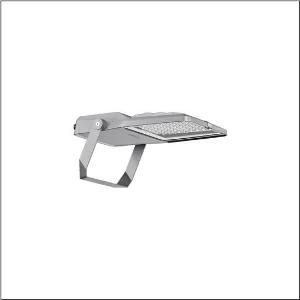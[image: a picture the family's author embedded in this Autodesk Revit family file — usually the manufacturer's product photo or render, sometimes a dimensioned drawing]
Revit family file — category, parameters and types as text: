
# Revit family: floodlight_fl_21_iq_mini___pl33t_5xa7771d4f1a_3e9c
name_source: partatom
category: Lighting Fixtures
units: mm (PartAtom-declared; Revit-internal decimal feet)

## family parameters
Cut with Voids When Loaded = No
Host = Face
Light Source = No
Part Type = Normal
Room Calculation Point = No
Round Connector Dimension = Use Diameter
Shared = No

## types (1)
- --- (1 x LED, 18390 lm, 143 W, 4000K)
    Apparent Load = 143 VA
    CIE Flux Codes = 26 75 99 100 100
    Color Rendering = 70
    Color Temperature = 4000K
    Default Elevation = 1800 mm
    Description = Floodlight FL 21 iQ mini, floodlight, primary light control with lens, of PMMA, primary optical cover: protective disc, of toughened safety glass, transparent, light distribution: PL33T, light emission: direct distribution, installation type: surface-mounted, LED, High Power LED, rated luminous flux: 18.390lm, luminous efficacy: 129lm/W, light colour: 740, colour temperature: 4000K, control: Auto-Match, Temp-Guard, Lumen-Switch, Night-Set, Smart-Wire, Light-Fading, Desk-Remote (wireless, voltage-free reading and setting of iQ features in the workshop via application-optimized NFC function/RFID function), optimised constant luminous flux control (CLO 2.0), with terminal, 6-pole, mains connection: 220..240V, AC, 50/60Hz, start of lifetime: 143W, end of service life: 152W, reduction: 61W, luminaire housing, of diecast aluminium, powder-coated, Siteco® metallic grey (DB 702S), corrosivity category C5 mid according to DIN EN ISO 12944, sealing non-destructively replaceable, mounting bracket, of steel, galvanised, powder-coated, Siteco® metallic grey (DB 702S), protection rating (complete): IP66, insulation class (complete): insulation class II (safety insulation), certification: CE, ENEC, VDE, protection symbol: D, impact resistance: IK08, permissible operating ambient temperature: -40..+40°C, permissible operating ambient temperature for outdoor applications: -40..+50°C, standard: DIN EN 12944, LABS conformity tested according to VDMA 24364:2018-05, packaging unit: 1 piece

Light Distribution: PL33T
    Height = 70 mm
    Lamp = 1 x LED
    Lamp Light Flux = 18390 lm
    Lamp Power = 143 W
    Lamp count = 1
    Length = 485 mm
    Luminous efficacy = 129 lm/W
    Manufacturer = Siteco
    ModVariant = No
    Model = 5XA7771D4F1A
    Number of Poles = 1
    OnlyDefault = Yes
    Power Factor = 1
    Product Name = Floodlight FL 21 iQ mini | PL33T
    Product group = floodlight | pylon annexe
    ProductGroupID = 6200
    Protection Class = Protection class II
    Protection Degree = IP 66
    RLX_Detail_Level = 1
    RLX_Emergency_Light_Flux = 0 lm
    RLX_Emergency_Type = 0
    RLX_Emergency_Type_DB = No
    RlxData = <blob elided: 96325 chars, md5=e342ebd0>
    Socket = socket
    Standby Power = 0 W
    System Light Flux = 18390 lm
    System Power = 143 W
    Type Comments = factory setting: luminous flux: 100 % | dim-lin: 254 | 730 mA
    Type Image = l_1006845.jpg
    URL = http://relux.com
    VarID = @adj_099317
    Voltage = 0 V
    Weight = 0.00 kg
    Width = 337 mm

## geometry (parser evidence)
native form markers: Blend x4, Sweep x12
no freeform markers — native parametric forms only
